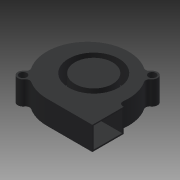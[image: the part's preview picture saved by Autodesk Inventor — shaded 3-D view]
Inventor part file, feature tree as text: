
AUTODESK INVENTOR PART (.ipt)
format: ipt  version: 2013 (Build 170138000, 138)  size: 141,824 bytes
history: native  units: mm
features: extrude x3, sketch x3
ambient origin geometry x8: Origin, YZ Plane, XZ Plane, XY Plane, X Axis, Y Axis, Z Axis, Center Point
bodies: Solid1 (feature_tree)
feature tree (6):
  extrude  "Extrusion1"  Depth=15.0mm TaperAngle=0.0deg
  extrude  "Extrusion2"  Depth=24.0mm
  extrude  "Extrusion3"  Depth=14.0mm TaperAngle=0.0deg
  sketch  "Sketch1"  dims[d6=4.8mm d7=29.0mm d8=20.0mm d9=2.5mm d10=2.5mm d11=2.5mm d12=15.0mm d13=0.0mm]
  sketch  "Sketch2"  dims[d14=15.0mm d15=0.0mm d16=24.0mm]
  sketch  "Sketch3"  dims[d18=32.0mm d19=14.0mm d20=0.0mm]
